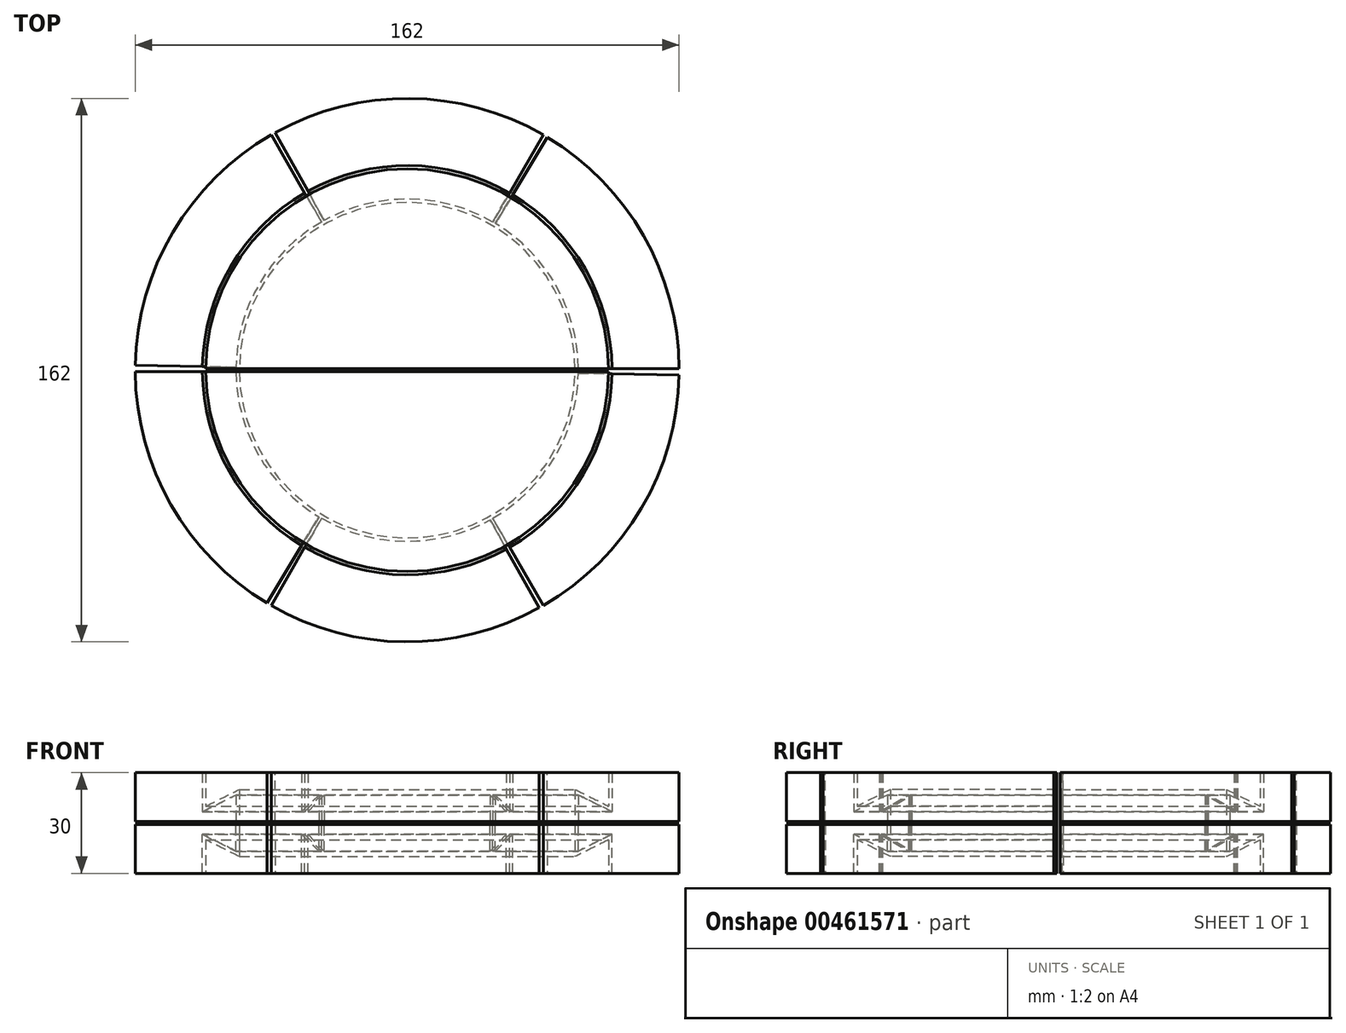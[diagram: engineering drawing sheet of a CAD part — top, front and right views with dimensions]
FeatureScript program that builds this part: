
annotation { "Feature Type Name" : "Feature", "Feature Type Description" : "" }
export const myFeature = defineFeature(function(context is Context, id is Id, definition is map)
    precondition{}
    {
        {
            var Q0;
            Q0=qCreatedBy(makeId("Front.planeOp"),FACE);
            var sketch = newSketch(context, id + "F0", { "sketchPlane" : qUnion([Q0])});
            skLineSegment(sketch, "E0", {"start": v(0, 74.8) * mm, "end": v(0, -71.2) * mm});
            skSolve(sketch);
        }
        {
            var Q0;
            Q0=qCreatedBy(makeId("Front.planeOp"),FACE);
            var sketch = newSketch(context, id + "F1", { "sketchPlane" : qUnion([Q0])});
            skLineSegment(sketch, "E1", {"start": v(0, 15) * mm, "end": v(-60, 15) * mm});
            skLineSegment(sketch, "E2", {"start": v(-60, 15) * mm, "end": v(-60, 5) * mm});
            skLineSegment(sketch, "E3", {"start": v(-60, 5) * mm, "end": v(-50, 10) * mm});
            skLineSegment(sketch, "E4", {"start": v(-50, 10) * mm, "end": v(-50, -10) * mm});
            skLineSegment(sketch, "E5", {"start": v(-50, -10) * mm, "end": v(-60, -5) * mm});
            skLineSegment(sketch, "E6", {"start": v(-60, -5) * mm, "end": v(-60, -15) * mm});
            skLineSegment(sketch, "E7", {"start": v(-60, -15) * mm, "end": v(0, -15) * mm});
            skLineSegment(sketch, "E8", {"start": v(0, -15) * mm, "end": v(0, 0) * mm});
            skLineSegment(sketch, "E9", {"start": v(0, 0) * mm, "end": v(0, 15) * mm});
            skSolve(sketch);
        }
        {
            var Q0;
            Q0 = qSketchRegion(id + "F1", true);
            var Q1;
            Q1=sQuery(id+"F1.wireOp",EDGE,"E9");
            revolve(context, id + "F2", {"entities" : qUnion([Q0]), "axis" : qUnion([Q1]), "revolveType" : RevolveType.ONE_DIRECTION, "angle" : 180 * degree});
        }
        {
            var Q0;
            Q0=qCreatedBy(makeId("Front.planeOp"),FACE);
            var sketch = newSketch(context, id + "F3", { "sketchPlane" : qUnion([Q0])});
            skLineSegment(sketch, "E10", {"start": v(0, 15) * mm, "end": v(-60, 15) * mm, "construction": true});
            skLineSegment(sketch, "E11", {"start": v(-60, 15) * mm, "end": v(-60, 5) * mm, "construction": true});
            skLineSegment(sketch, "E12", {"start": v(-60, 5) * mm, "end": v(-50, 10) * mm, "construction": true});
            skLineSegment(sketch, "E13", {"start": v(-50, 0) * mm, "end": v(-50, -10) * mm, "construction": true});
            skLineSegment(sketch, "E14", {"start": v(-50, -10) * mm, "end": v(-60, -5) * mm, "construction": true});
            skLineSegment(sketch, "E15", {"start": v(-60, -5) * mm, "end": v(-60, -15) * mm, "construction": true});
            skLineSegment(sketch, "E16", {"start": v(-60, -15) * mm, "end": v(0, -15) * mm, "construction": true});
            skLineSegment(sketch, "E17", {"start": v(0, -15) * mm, "end": v(0, 0) * mm, "construction": true});
            skLineSegment(sketch, "E18", {"start": v(0, 0) * mm, "end": v(0, 15) * mm, "construction": true});
            skPoint(sketch, "E19", {"position": v(-50, 0) * mm});
            skLineSegment(sketch, "E20", {"start": v(-50, 10) * mm, "end": v(-50, 0) * mm, "construction": true});
            skLineSegment(sketch, "E21.0", {"start": v(-51, 8.38) * mm, "end": v(-51, 0.5) * mm});
            skLineSegment(sketch, "E21.1", {"start": v(-61, 3.38) * mm, "end": v(-51, 8.38) * mm});
            skLineSegment(sketch, "E21.2", {"start": v(-61, 15) * mm, "end": v(-61, 3.38) * mm});
            skLineSegment(sketch, "E22", {"start": v(-51, 0.5) * mm, "end": v(-81, 0.5) * mm});
            skLineSegment(sketch, "E23", {"start": v(-81, 0.5) * mm, "end": v(-81, 15) * mm});
            skLineSegment(sketch, "E24", {"start": v(-81, 15) * mm, "end": v(-61, 15) * mm});
            skSolve(sketch);
        }
        {
            var Q0;
            Q0 = qSketchRegion(id + "F3", true);
            var Q1;
            Q1=sQuery(id+"F3.wireOp",EDGE,"E18");
            revolve(context, id + "F4", {"entities" : qUnion([Q0]), "axis" : qUnion([Q1]), "revolveType" : RevolveType.ONE_DIRECTION, "angle" : 59 * degree});
        }
        {
            var Q0;
            Q0=makeQuery(id+"F2.opRevolve","SWEPT_BODY",BODY,{"disambiguationData":[OSD([sQuery(id+"F1.wireOp",EDGE,"E1"),sQuery(id+"F1.wireOp",EDGE,"E2"),sQuery(id+"F1.wireOp",EDGE,"E3"),sQuery(id+"F1.wireOp",EDGE,"E4"),sQuery(id+"F1.wireOp",EDGE,"E5"),sQuery(id+"F1.wireOp",EDGE,"E6"),sQuery(id+"F1.wireOp",EDGE,"E7"),sQuery(id+"F1.wireOp",EDGE,"E8"),sQuery(id+"F1.wireOp",EDGE,"E9")])]});
            var Q1;
            Q1=sQuery(id+"F0.wireOp",EDGE,"E0");
            circularPattern(context, id + "F5", {"entities" : qUnion([Q0]), "axis" : qUnion([Q1]), "angle" : 360 * degree, "instanceCount" : 2, "equalSpace" : true});
        }
        {
            var Q0;
            Q0=makeQuery(id+"F4.opRevolve","SWEPT_BODY",BODY,{"disambiguationData":[OSD([sQuery(id+"F3.wireOp",EDGE,"E21.0"),sQuery(id+"F3.wireOp",EDGE,"E21.1"),sQuery(id+"F3.wireOp",EDGE,"E21.2"),sQuery(id+"F3.wireOp",EDGE,"E22"),sQuery(id+"F3.wireOp",EDGE,"E23"),sQuery(id+"F3.wireOp",EDGE,"E24")])]});
            var Q1;
            Q1=sQuery(id+"F0.wireOp",EDGE,"E0");
            circularPattern(context, id + "F6", {"entities" : qUnion([Q0]), "axis" : qUnion([Q1]), "angle" : 360 * degree, "instanceCount" : 6, "equalSpace" : true});
        }
        {
            var Q0;
            Q0=makeQuery(id+"F6.opPattern","COPY",BODY,{"derivedFrom":makeQuery(id+"F4.opRevolve","SWEPT_BODY",BODY,{"disambiguationData":[OSD([sQuery(id+"F3.wireOp",EDGE,"E21.0"),sQuery(id+"F3.wireOp",EDGE,"E21.1"),sQuery(id+"F3.wireOp",EDGE,"E21.2"),sQuery(id+"F3.wireOp",EDGE,"E22"),sQuery(id+"F3.wireOp",EDGE,"E23"),sQuery(id+"F3.wireOp",EDGE,"E24")])]}),"instanceName":"5"});
            var Q1;
            Q1=makeQuery(id+"F6.opPattern","COPY",BODY,{"derivedFrom":makeQuery(id+"F4.opRevolve","SWEPT_BODY",BODY,{"disambiguationData":[OSD([sQuery(id+"F3.wireOp",EDGE,"E21.0"),sQuery(id+"F3.wireOp",EDGE,"E21.1"),sQuery(id+"F3.wireOp",EDGE,"E21.2"),sQuery(id+"F3.wireOp",EDGE,"E22"),sQuery(id+"F3.wireOp",EDGE,"E23"),sQuery(id+"F3.wireOp",EDGE,"E24")])]}),"instanceName":"4"});
            var Q2;
            Q2=makeQuery(id+"F6.opPattern","COPY",BODY,{"derivedFrom":makeQuery(id+"F4.opRevolve","SWEPT_BODY",BODY,{"disambiguationData":[OSD([sQuery(id+"F3.wireOp",EDGE,"E21.0"),sQuery(id+"F3.wireOp",EDGE,"E21.1"),sQuery(id+"F3.wireOp",EDGE,"E21.2"),sQuery(id+"F3.wireOp",EDGE,"E22"),sQuery(id+"F3.wireOp",EDGE,"E23"),sQuery(id+"F3.wireOp",EDGE,"E24")])]}),"instanceName":"3"});
            var Q3;
            Q3=makeQuery(id+"F6.opPattern","COPY",BODY,{"derivedFrom":makeQuery(id+"F4.opRevolve","SWEPT_BODY",BODY,{"disambiguationData":[OSD([sQuery(id+"F3.wireOp",EDGE,"E21.0"),sQuery(id+"F3.wireOp",EDGE,"E21.1"),sQuery(id+"F3.wireOp",EDGE,"E21.2"),sQuery(id+"F3.wireOp",EDGE,"E22"),sQuery(id+"F3.wireOp",EDGE,"E23"),sQuery(id+"F3.wireOp",EDGE,"E24")])]}),"instanceName":"2"});
            var Q4;
            Q4=makeQuery(id+"F6.opPattern","COPY",BODY,{"derivedFrom":makeQuery(id+"F4.opRevolve","SWEPT_BODY",BODY,{"disambiguationData":[OSD([sQuery(id+"F3.wireOp",EDGE,"E21.0"),sQuery(id+"F3.wireOp",EDGE,"E21.1"),sQuery(id+"F3.wireOp",EDGE,"E21.2"),sQuery(id+"F3.wireOp",EDGE,"E22"),sQuery(id+"F3.wireOp",EDGE,"E23"),sQuery(id+"F3.wireOp",EDGE,"E24")])]}),"instanceName":"1"});
            var Q5;
            Q5=makeQuery(id+"F4.opRevolve","SWEPT_BODY",BODY,{"disambiguationData":[OSD([sQuery(id+"F3.wireOp",EDGE,"E21.0"),sQuery(id+"F3.wireOp",EDGE,"E21.1"),sQuery(id+"F3.wireOp",EDGE,"E21.2"),sQuery(id+"F3.wireOp",EDGE,"E22"),sQuery(id+"F3.wireOp",EDGE,"E23"),sQuery(id+"F3.wireOp",EDGE,"E24")])]});
            var Q6;
            Q6=qCreatedBy(makeId("Top.planeOp"),FACE);
            mirror(context, id + "F7", {"entities" : qUnion([Q0, Q1, Q2, Q3, Q4, Q5]), "mirrorPlane" : qUnion([Q6])});
        }
        {
            var Q0;
            Q0=qCreatedBy(makeId("Front.planeOp"),FACE);
            var sketch = newSketch(context, id + "F8", { "sketchPlane" : qUnion([Q0])});
            skLineSegment(sketch, "E25.bottom", {"start": v(-100, 50) * mm, "end": v(100, 50) * mm});
            skLineSegment(sketch, "E25.top", {"start": v(-100, -50) * mm, "end": v(100, -50) * mm});
            skLineSegment(sketch, "E25.left", {"start": v(-100, 50) * mm, "end": v(-100, -50) * mm});
            skLineSegment(sketch, "E25.right", {"start": v(100, 50) * mm, "end": v(100, -50) * mm});
            skSolve(sketch);
        }
        {
            var Q0;
            Q0 = qSketchRegion(id + "F8", true);
            extrude(context, id + "F9", {"entities" : qUnion([Q0]), "operationType" : NewBodyOperationType.REMOVE, "endBound" : BoundingType.SYMMETRIC, "depth" : 1 * mm});
        }
    });
